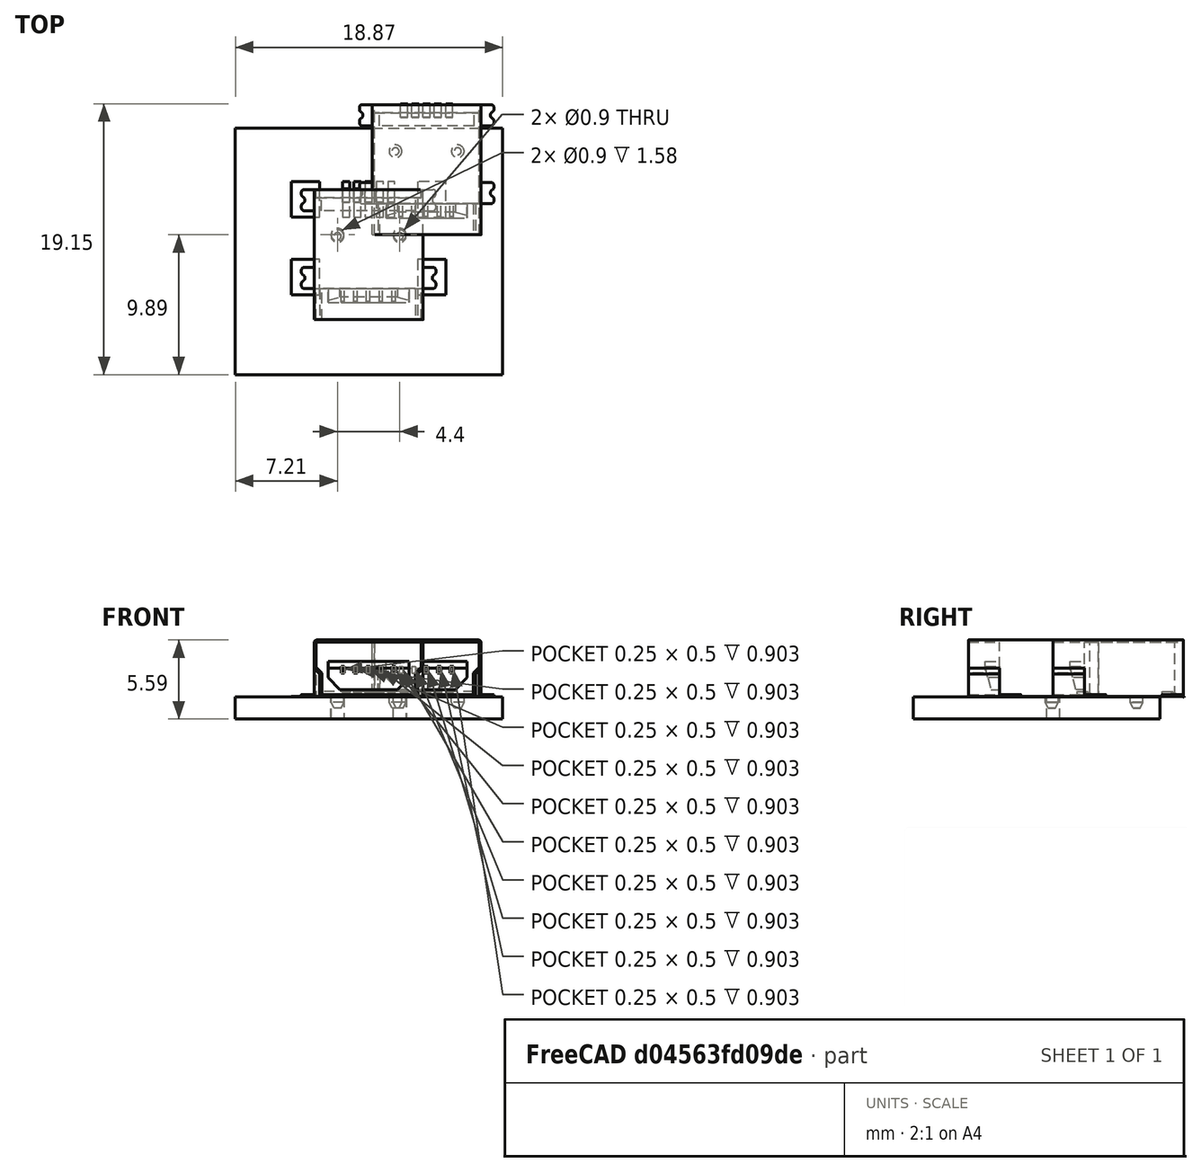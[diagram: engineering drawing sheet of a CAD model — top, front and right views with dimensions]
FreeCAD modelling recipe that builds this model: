
FCSTD DOCUMENT  (FreeCAD 0.18.4R)
Label: Sunrom-4293
License: All rights reserved
LicenseURL: http://en.wikipedia.org/wiki/All_rights_reserved
objects: Part::Box×32, Part::Cut×24, Part::Cylinder×6, Part::MultiFuse×6, Part::FeaturePython×6, Part::Fillet×5, Part::Cone×2, Part::Mirroring×1, App::DocumentObjectGroup×1, Part::Feature×1
note: 83 computed .brp shape members not serialized (recipe doc carries the construction recipe); baked Part::Feature solids carry a one-line shape summary decoded from their .brp

FEATURE [Part::Box] Box013  label="Cube009"
  AttacherType = Attacher::AttachEngine3D
  Height = 1.91
  Length = 0.4
  Placement = pos=(0.15,-0.1,0.15) rot=(0,0,1;0rad)
  Width = 2.3
FEATURE [Part::Box] Box014  label="Cube010"
  AttacherType = Attacher::AttachEngine3D
  Height = 1.91
  Length = 0.4
  Placement = pos=(7,-0.1,0.15) rot=(0,0,1;0rad)
  Width = 2.3
FEATURE [Part::Box] Box015  label="Cube011"
  AttacherType = Attacher::AttachEngine3D
  Height = 0.8
  Length = 0.8
  Placement = pos=(7.4,-0.1,2.06) rot=(0,1,0;3.92699rad)
  Width = 9.4
FEATURE [Part::Cut] Cut013
  Base = -> Box014
  Placement = pos=(0.15,0,0) rot=(0,0,1;0rad)
  Tool = -> Box015
FEATURE [Part::Box] Box017  label="Cube013"
  AttacherType = Attacher::AttachEngine3D
  Height = 0.8
  Length = 0.8
  Placement = pos=(0.15,-0.1,2.06) rot=(0,1,0;0.785398rad)
  Width = 9.4
FEATURE [Part::Box] Box018  label="Cube014"
  AttacherType = Attacher::AttachEngine3D
  Height = 3.7
  Length = 7.4
  Placement = pos=(0.15,-0.1,0.15) rot=(0,0,1;0rad)
  Width = 9.4
FEATURE [Part::Box] Box019  label="Cube015"
  AttacherType = Attacher::AttachEngine3D
  Height = 4
  Length = 7.7
  Width = 9.2
FEATURE [Part::Box] Box020  label="Cube016"
  AttacherType = Attacher::AttachEngine3D
  Height = 0.8
  Length = 0.8
  Placement = pos=(0,0,2) rot=(0,1,0;0.785398rad)
  Width = 2.2
FEATURE [Part::Box] Box021  label="Cube017"
  AttacherType = Attacher::AttachEngine3D
  Height = 2
  Length = 0.4
  Width = 2.2
FEATURE [Part::Cut] Cut020  label="Left Side Cutout001"
  Base = -> Box021
  Tool = -> Box020
FEATURE [Part::Cut] Cut019
  Base = -> Box019
  Tool = -> Cut020
FEATURE [Part::Box] Box022  label="Cube018"
  AttacherType = Attacher::AttachEngine3D
  Height = 2
  Length = 0.4
  Width = 2.2
FEATURE [Part::Box] Box023  label="Cube019"
  AttacherType = Attacher::AttachEngine3D
  Height = 0.8
  Length = 0.8
  Placement = pos=(0,0,2) rot=(0,1,0;0.785398rad)
  Width = 2.2
FEATURE [Part::Cut] Cut018  label="Right Side Cutout001"
  Base = -> Box022
  Placement = pos=(7.7,0,0) rot=(0,0,1;0rad)
  Tool = -> Box023
FEATURE [Part::Mirroring] Part__Mirroring001  label="Right Side Cutout (Mirror #1)001"
  Base = (7.7,0,0)
  Normal = (1,0,0)
  Source = -> Cut018
FEATURE [Part::Cut] Cut017
  Base = -> Cut019
  Tool = -> Part__Mirroring001
FEATURE [Part::Fillet] Fillet009  label="Body001"
  Base = -> Cut017
  Edges = 2 edges r=0.2: [Edge2,Edge15]
FEATURE [Part::Box] Box024  label="Foot015"
  AttacherType = Attacher::AttachEngine3D
  Height = 0.15
  Length = 0.9
  Placement = pos=(-0.9,2.2,0) rot=(0,0,1;0rad)
  Width = 1.5
FEATURE [Part::Box] Box025  label="Foot016"
  AttacherType = Attacher::AttachEngine3D
  Height = 0.15
  Length = 0.9
  Placement = pos=(-0.9,7.7,0) rot=(0,0,1;0rad)
  Width = 1.5
FEATURE [Part::Box] Box026  label="Foot017"
  AttacherType = Attacher::AttachEngine3D
  Height = 0.15
  Length = 0.9
  Placement = pos=(7.7,2.2,0) rot=(0,0,1;0rad)
  Width = 1.5
FEATURE [Part::Box] Box027  label="Foot018"
  AttacherType = Attacher::AttachEngine3D
  Height = 0.15
  Length = 0.9
  Placement = pos=(7.7,7.7,0) rot=(0,0,1;0rad)
  Width = 1.5
FEATURE [Part::Cylinder] Cylinder004
  Angle = 360
  AttacherType = Attacher::AttachEngine3D
  Height = 0.17
  Placement = pos=(-0.9,2.95,-0.01) rot=(0,0,1;0rad)
  Radius = 0.25
FEATURE [Part::Cylinder] Cylinder005
  Angle = 360
  AttacherType = Attacher::AttachEngine3D
  Height = 0.17
  Placement = pos=(8.6,2.95,-0.01) rot=(0,0,1;0rad)
  Radius = 0.25
FEATURE [Part::Cut] Cut014  label="Foot008"
  Base = -> Box026
  Tool = -> Cylinder005
FEATURE [Part::Fillet] Fillet008  label="Foot014"
  Base = -> Cut014
  Edges = 4 edges r=0.2: [Edge6,Edge13,Edge17,Edge18]
FEATURE [Part::Cut] Cut021  label="Foot019"
  Base = -> Box024
  Tool = -> Cylinder004
FEATURE [Part::Fillet] Fillet006  label="Foot012"
  Base = -> Cut021
  Edges = 4 edges r=0.2: [Edge2,Edge4,Edge19,Edge20]
FEATURE [Part::Cylinder] Cylinder006
  Angle = 360
  AttacherType = Attacher::AttachEngine3D
  Height = 0.17
  Placement = pos=(-0.9,8.45,-0.01) rot=(0,0,1;0rad)
  Radius = 0.25
FEATURE [Part::Cut] Cut016  label="Foot011"
  Base = -> Box025
  Tool = -> Cylinder006
FEATURE [Part::Fillet] Fillet007  label="Foot013"
  Base = -> Cut016
  Edges = 4 edges r=0.2: [Edge2,Edge4,Edge19,Edge20]
FEATURE [Part::Cylinder] Cylinder007
  Angle = 360
  AttacherType = Attacher::AttachEngine3D
  Height = 0.17
  Placement = pos=(8.6,8.45,-0.01) rot=(0,0,1;0rad)
  Radius = 0.25
FEATURE [Part::Cut] Cut015  label="Foot010"
  Base = -> Box027
  Tool = -> Cylinder007
FEATURE [Part::Fillet] Fillet005  label="Foot009"
  Base = -> Cut015
  Edges = 4 edges r=0.2: [Edge6,Edge13,Edge17,Edge18]
FEATURE [Part::MultiFuse] Fusion001  label="Main Body001"
  Shapes = -> [Fillet009,Fillet006,Fillet007,Fillet008,Fillet005]
FEATURE [Part::Cut] Cut022
  Base = -> Box013
  Tool = -> Box017
FEATURE [Part::Cut] Cut023
  Base = -> Box018
  Tool = -> Cut022
FEATURE [Part::Cut] Cut024
  Base = -> Cut023
  Tool = -> Cut013
FEATURE [Part::Cut] Cut025  label="Shell"
  Base = -> Fusion001
  Tool = -> Cut024
FEATURE [Part::Box] Box  label="Cube"
  AttacherType = Attacher::AttachEngine3D
  Height = 0.2
  Length = 7.4
  Placement = pos=(0.15,2.2,-0.01) rot=(0,0,1;0rad)
  Width = 7
FEATURE [Part::Cut] Cut  label="Metal Shell"
  Base = -> Cut025
  Tool = -> Box
FEATURE [Part::Box] Box028  label="Cube020"
  AttacherType = Attacher::AttachEngine3D
  Height = 3.85
  Length = 7.4
  Placement = pos=(0.15,2.2,0) rot=(0,0,1;0rad)
  Width = 7
FEATURE [Part::Cylinder] Cylinder
  Angle = 360
  AttacherType = Attacher::AttachEngine3D
  Height = 0.4
  Placement = pos=(1.65,5.9,-0.4) rot=(0,0,1;0rad)
  Radius = 0.45
FEATURE [Part::Cylinder] Cylinder008
  Angle = 360
  AttacherType = Attacher::AttachEngine3D
  Height = 0.4
  Placement = pos=(6.05,5.9,-0.4) rot=(0,0,1;0rad)
  Radius = 0.45
FEATURE [Part::Cone] Cone
  Angle = 360
  AttacherType = Attacher::AttachEngine3D
  Height = 0.4
  Placement = pos=(1.65,5.9,-0.8) rot=(0,0,1;0rad)
  Radius1 = 0.25
  Radius2 = 0.45
FEATURE [Part::Cone] Cone001
  Angle = 360
  AttacherType = Attacher::AttachEngine3D
  Height = 0.4
  Placement = pos=(6.05,5.9,-0.8) rot=(0,0,1;0rad)
  Radius1 = 0.25
  Radius2 = 0.45
FEATURE [Part::MultiFuse] Fusion
  Shapes = -> [Cylinder,Cone]
FEATURE [Part::MultiFuse] Fusion002
  Shapes = -> [Cylinder008,Cone001]
FEATURE [Part::Box] Box029  label="Cube021"
  AttacherType = Attacher::AttachEngine3D
  Height = 2
  Length = 5.7
  Placement = pos=(1,0.65,0.2) rot=(1,0,0;0.261799rad)
  Width = 1
FEATURE [Part::Box] Box030  label="Cube022"
  AttacherType = Attacher::AttachEngine3D
  Height = 2
  Length = 5.7
  Placement = pos=(1,1.2,0.5) rot=(1,0,0;0rad)
  Width = 1
FEATURE [Part::MultiFuse] Fusion003
  Shapes = -> [Box028,Fusion]
FEATURE [Part::MultiFuse] Fusion004
  Shapes = -> [Fusion003,Fusion002]
FEATURE [Part::Cut] Cut026
  Base = -> Box030
  Tool = -> Box029
FEATURE [Part::Box] Box031  label="Cube023"
  AttacherType = Attacher::AttachEngine3D
  Height = 2
  Length = 2
  Placement = pos=(-0.5,0,0) rot=(0,1,0;0.785398rad)
  Width = 3
FEATURE [Part::Box] Box032  label="Cube024"
  AttacherType = Attacher::AttachEngine3D
  Height = 2
  Length = 2
  Placement = pos=(6.8,0,-1.4) rot=(0,-1,0;0.785398rad)
  Width = 3
FEATURE [Part::Cut] Cut027
  Base = -> Cut026
  Tool = -> Box031
FEATURE [Part::Cut] Cut028
  Base = -> Cut027
  Tool = -> Box032
FEATURE [Part::Box] Box033  label="Cube025"
  AttacherType = Attacher::AttachEngine3D
  Height = 0.5
  Length = 0.25
  Placement = pos=(1.9,0.1,1.65) rot=(0,0,1;0rad)
  Width = 2.2
FEATURE [Part::Box] Box034  label="Cube026"
  AttacherType = Attacher::AttachEngine3D
  Height = 0.5
  Length = 0.25
  Placement = pos=(2.8,0.1,1.65) rot=(0,0,1;0rad)
  Width = 2.2
FEATURE [Part::Box] Box035  label="Cube027"
  AttacherType = Attacher::AttachEngine3D
  Height = 0.5
  Length = 0.25
  Placement = pos=(3.7,0.1,1.65) rot=(0,0,1;0rad)
  Width = 2.2
FEATURE [Part::Box] Box036  label="Cube028"
  AttacherType = Attacher::AttachEngine3D
  Height = 0.5
  Length = 0.25
  Placement = pos=(4.6,0.1,1.65) rot=(0,0,1;0rad)
  Width = 2.2
FEATURE [Part::Box] Box037  label="Cube029"
  AttacherType = Attacher::AttachEngine3D
  Height = 0.5
  Length = 0.25
  Placement = pos=(5.5,0.1,1.65) rot=(0,0,1;0rad)
  Width = 2.2
FEATURE [Part::Cut] Cut029
  Base = -> Cut028
  Tool = -> Box033
FEATURE [Part::Cut] Cut030
  Base = -> Cut029
  Tool = -> Box034
FEATURE [Part::Cut] Cut031
  Base = -> Cut030
  Tool = -> Box035
FEATURE [Part::Cut] Cut032
  Base = -> Cut031
  Tool = -> Box036
FEATURE [Part::Cut] Cut033
  Base = -> Cut032
  Tool = -> Box037
FEATURE [Part::MultiFuse] Fusion005
  Shapes = -> [Cut033,Fusion004]
FEATURE [Part::Box] Box038  label="Cube030"
  AttacherType = Attacher::AttachEngine3D
  Height = 0.45
  Length = 6.7
  Placement = pos=(0.5,7.7,-0.1) rot=(0,0,1;0rad)
  Width = 2
FEATURE [Part::Cut] Cut034
  Base = -> Fusion005
  Tool = -> Box038
FEATURE [Part::Box] Box039  label="Cube031"
  AttacherType = Attacher::AttachEngine3D
  Height = 3.95
  Length = 7.4
  Placement = pos=(0.15,8.6,-0.1) rot=(0,0,1;0rad)
  Width = 1
FEATURE [Part::Cut] Cut035  label="Plastic Guts"
  Base = -> Cut034
  Tool = -> Box039
FEATURE [Part::Box] Box040  label="Cube032"
  AttacherType = Attacher::AttachEngine3D
  Height = 0.05
  Length = 0.5
  Placement = pos=(2,8.3,0.3) rot=(-1,0,0;0.349066rad)
  Width = 1
FEATURE [Part::Box] Box041  label="Cube033"
  AttacherType = Attacher::AttachEngine3D
  Height = 0.05
  Length = 0.5
  Placement = pos=(2.8,8.3,0.3) rot=(-1,0,0;0.349066rad)
  Width = 1
FEATURE [Part::Box] Box042  label="Cube034"
  AttacherType = Attacher::AttachEngine3D
  Height = 0.05
  Length = 0.5
  Placement = pos=(3.6,8.3,0.3) rot=(-1,0,0;0.349066rad)
  Width = 1
FEATURE [Part::Box] Box043  label="Cube035"
  AttacherType = Attacher::AttachEngine3D
  Height = 0.05
  Length = 0.5
  Placement = pos=(4.4,8.3,0.3) rot=(-1,0,0;0.349066rad)
  Width = 1
FEATURE [Part::Box] Box044  label="Cube036"
  AttacherType = Attacher::AttachEngine3D
  Height = 0.05
  Length = 0.5
  Placement = pos=(5.2,8.3,0.3) rot=(-1,0,0;0.349066rad)
  Width = 1
FEATURE [Part::FeaturePython] FCrtYd_lines  label="FCrtYd"  # a2plus imported part (geometry in sourceFile) (typed FeaturePython)
  fixedPosition = true
FEATURE [Part::FeaturePython] FFab_lines  label="FFab"  # a2plus imported part (geometry in sourceFile) (typed FeaturePython)
  fixedPosition = true
FEATURE [Part::FeaturePython] Filk_lines  label="FrontSilk"  # a2plus imported part (geometry in sourceFile) (typed FeaturePython)
  fixedPosition = true
FEATURE [Part::FeaturePython] TopPads  # a2plus imported part (geometry in sourceFile) (typed FeaturePython)
  fixedPosition = true
FEATURE [Part::FeaturePython] THPs  label="PTHs"  # a2plus imported part (geometry in sourceFile) (typed FeaturePython)
  fixedPosition = true
FEATURE [Part::FeaturePython] newPCB  label="Pcb"  # a2plus imported part (geometry in sourceFile) (typed FeaturePython)
  fixedPosition = true
FEATURE [App::DocumentObjectGroup] _module_fp
  Group = -> [FCrtYd_lines,FFab_lines,Filk_lines,TopPads,THPs,newPCB]
FEATURE [Part::Feature] Shape  label="Sunrom 4293 Mini USB Female"
  shape: bbox 9.5 x 9.257 x 4.8 mm, 155 faces, 6 solids (baked)
